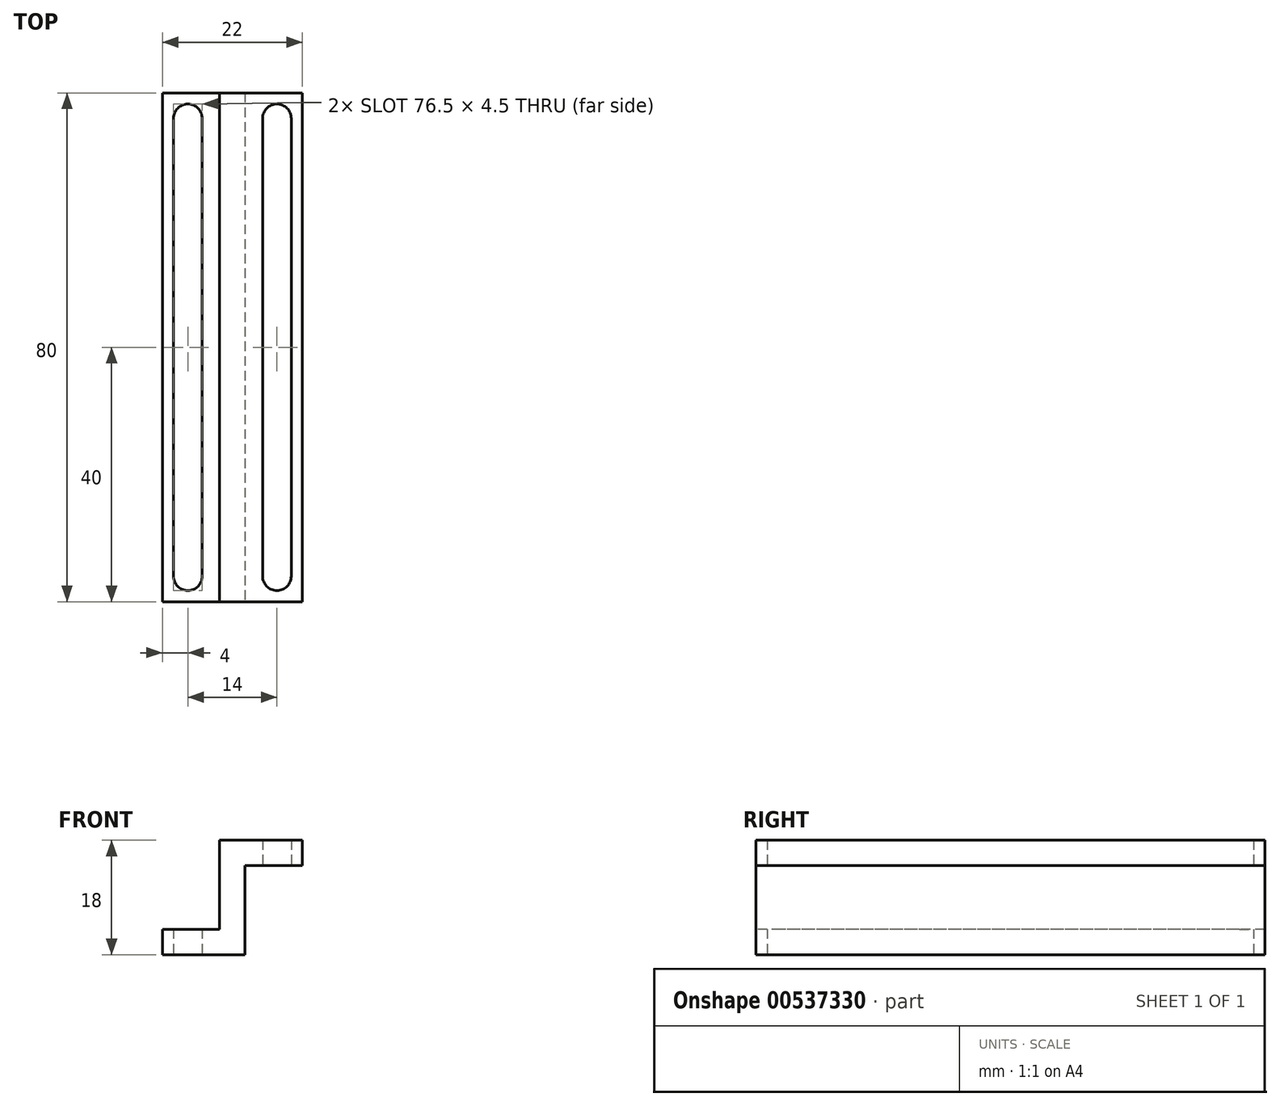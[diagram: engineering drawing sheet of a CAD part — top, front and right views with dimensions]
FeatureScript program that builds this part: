
annotation { "Feature Type Name" : "Feature", "Feature Type Description" : "" }
export const myFeature = defineFeature(function(context is Context, id is Id, definition is map)
    precondition{}
    {
        {
            var Q0;
            Q0=qCreatedBy(makeId("Top.planeOp"),FACE);
            var sketch = newSketch(context, id + "F0", { "sketchPlane" : qUnion([Q0])});
            skLineSegment(sketch, "E0.bottom", {"start": v(11, 40) * mm, "end": v(-11, 40) * mm});
            skLineSegment(sketch, "E0.top", {"start": v(11, -40) * mm, "end": v(-11, -40) * mm});
            skLineSegment(sketch, "E0.left", {"start": v(11, 40) * mm, "end": v(11, -40) * mm});
            skLineSegment(sketch, "E0.right", {"start": v(-11, 40) * mm, "end": v(-11, -40) * mm});
            skPoint(sketch, "E0.middle", {"position": v(0, 0) * mm});
            skLineSegment(sketch, "E1", {"start": v(-2, 40) * mm, "end": v(-2, -40) * mm});
            skLineSegment(sketch, "E2", {"start": v(2, 40) * mm, "end": v(2, -40) * mm});
            skCircle(sketch, "E3", {"center": v(-7, 36) * mm, "radius": 2.25 * mm});
            skCircle(sketch, "E4", {"center": v(7, 36) * mm, "radius": 2.25 * mm});
            skCircle(sketch, "E5", {"center": v(-7, -36) * mm, "radius": 2.25 * mm});
            skCircle(sketch, "E6", {"center": v(7, -36) * mm, "radius": 2.25 * mm});
            skLineSegment(sketch, "E7", {"start": v(9.25, 36) * mm, "end": v(9.25, -36) * mm});
            skLineSegment(sketch, "E8", {"start": v(-9.25, 36) * mm, "end": v(-9.25, -36) * mm});
            skLineSegment(sketch, "E9", {"start": v(-4.75, 36) * mm, "end": v(-4.75, -36) * mm});
            skLineSegment(sketch, "E10", {"start": v(4.75, 36) * mm, "end": v(4.75, -36) * mm});
            skSolve(sketch);
        }
        {
            var Q0;
            {var subQ0=sQuery(id+"F0.wireOp",EDGE,"E0.right");Q0=makeQuery(id+"F0.imprint","IMPRINT",FACE,{"disambiguationData":[TD([[makeQuery(id+"F0.imprint","IMPRINT",EDGE,{"derivedFrom":subQ0}),1.0]])]});}
            extrude(context, id + "F1", {"entities" : qUnion([Q0]), "depth" : 4 * mm, "offsetDistance" : 25 * mm});
        }
        {
            var Q0;
            {var subQ0=sQuery(id+"F0.wireOp",EDGE,"E1");Q0=makeQuery(id+"F0.imprint","IMPRINT",FACE,{"disambiguationData":[TD([[makeQuery(id+"F0.imprint","IMPRINT",EDGE,{"derivedFrom":subQ0}),1.0]])]});}
            extrude(context, id + "F2", {"entities" : qUnion([Q0]), "operationType" : NewBodyOperationType.ADD, "depth" : 18 * mm, "offsetDistance" : 25 * mm});
        }
        {
            var Q0;
            {var subQ1=sQuery(id+"F0.wireOp",EDGE,"E0.left");Q0=makeQuery(id+"F0.imprint","IMPRINT",FACE,{"disambiguationData":[TD([[makeQuery(id+"F0.imprint","IMPRINT",EDGE,{"derivedFrom":subQ1}),-1.0]])]});}
            extrude(context, id + "F3", {"entities" : qUnion([Q0]), "operationType" : NewBodyOperationType.ADD, "depth" : 18 * mm, "offsetDistance" : 25 * mm, "hasSecondDirection" : true, "secondDirectionOppositeDirection" : true, "secondDirectionDepth" : -14 * mm});
        }
    });
